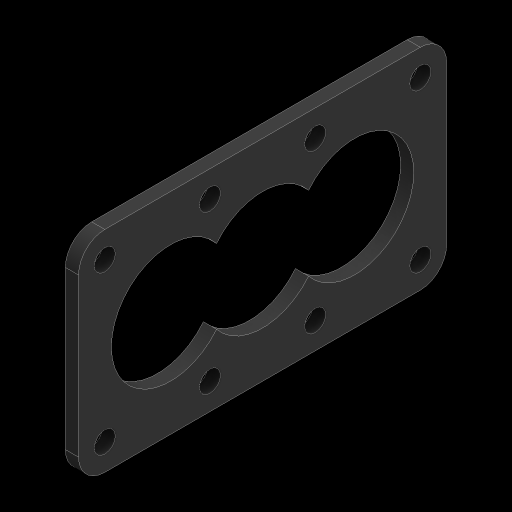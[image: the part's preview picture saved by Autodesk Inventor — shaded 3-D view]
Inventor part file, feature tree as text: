
AUTODESK INVENTOR PART (.ipt)
format: ipt  version: 2024 (Build 280153000, 153)  size: 149,504 bytes
history: native  units: in
note: dims shown in document units (in); Inventor stores cm internally (conversion verified against a paired STEP export)
features: sketch x3, hole x2, pattern_linear x2, extrude x1, fillet x1
ambient origin geometry x8: Origin, YZ Plane, XZ Plane, XY Plane, X Axis, Y Axis, Z Axis, Center Point
bodies: Solid1 (feature_tree)
feature tree (9):
  extrude  "RECTANGLE"  Depth=7.0in
  fillet  "FILLETS"  Radius=0.25in
  hole  "SMALL HOLE"  [1 undecoded]
  pattern_linear  "SMALL HOLES"  Count1=2 Spacing1=3.0in
  hole  "LARGE HOLE"  [1 undecoded]
  pattern_linear  "LARGE HOLES"  Spacing1=0.0in  [1 undecoded]
  sketch  "Sketch1"  dims[d0=4.0in d1=7.0in d2=0.25in d3=0.0in]
  sketch  "Sketch2"  dims[d4=0.5in]
  sketch  "Sketch3"  dims[d5=0.4in d6=0.75in d7=0.375in d8=0.25in d9=0.5635in d10=1.0in d11=0.8108in d12=1.5748in d14=2.0in d15=0.7874in d17=3.0in d18=2.25in d19=0.75in d20=0.375in d21=0.25in d22=0.5635in d23=1.0in d24=0.8108in d25=1.75in d26=0.0in d27=1.1811in d29=1.75in]
note: 3 required parameter values undecoded (feature->parameter linkage not recoverable at this tier; creation-order binding heuristic only, values carry confidence <= 0.55)
